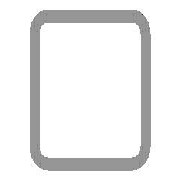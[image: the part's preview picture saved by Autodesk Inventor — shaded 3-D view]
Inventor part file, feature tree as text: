
AUTODESK INVENTOR PART (.ipt)
format: ipt  version: 2025.3 (Build 293356030, 356C)  size: 147,456 bytes
history: native  units: mm (DEFAULTED — no unit token found)
features: other x4, sketch x1, plane x1
ambient origin geometry x8: Origin, YZ Plane, XZ Plane, XY Plane, X Axis, Y Axis, Z Axis, Center Point
bodies: Solid1 (feature_tree), Body (feature_tree)
feature tree (6):
  parser-record x1  (decoder bookkeeping rows leaked as tree rows — omitted from the tree; the rows remain in map.json)
  other  "Driven Length"
  other  "Start Plane"
  other  "End Plane"
  sketch  "Sketch3"  dims[d3=230.0mm d4=0.0mm d7=4.0mm d9=40.0mm d11=40.0mm d12=2.0mm d13=-0.0mm d14=230.0mm d15=20.0mm d16=20.0mm d17=90.0deg d18=230.0mm]
  plane  "Work Plane3"
